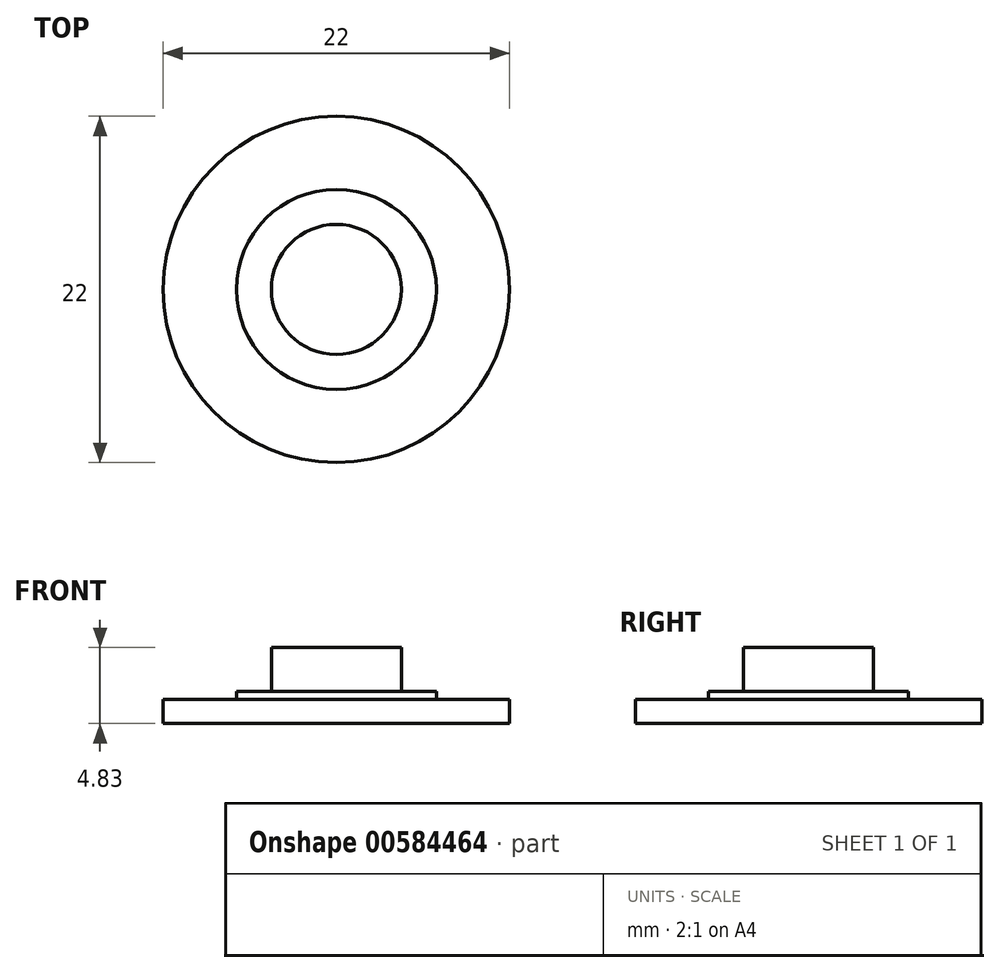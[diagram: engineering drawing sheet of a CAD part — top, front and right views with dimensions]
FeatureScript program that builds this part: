
annotation { "Feature Type Name" : "Feature", "Feature Type Description" : "" }
export const myFeature = defineFeature(function(context is Context, id is Id, definition is map)
    precondition{}
    {
        {
            var Q0;
            Q0=qCreatedBy(makeId("Top.planeOp"),FACE);
            var sketch = newSketch(context, id + "F0", { "sketchPlane" : qUnion([Q0])});
            skCircle(sketch, "E0", {"center": v(0, 0) * mm, "radius": 11 * mm});
            skSolve(sketch);
        }
        {
            var Q0;
            Q0=qSketchRegion(id+"F0",true);
            extrude(context, id + "F1", {"entities" : qUnion([Q0]), "depth" : 1.52 * mm, "offsetDistance" : 25.4 * mm});
        }
        {
            var Q0;
            Q0=makeQuery(id+"F1.opExtrude","CAP_FACE",FACE,{"disambiguationData":[OSD([sQuery(id+"F0.wireOp",EDGE,"E0")])],"isStart":false});
            var sketch = newSketch(context, id + "F2", { "sketchPlane" : qUnion([Q0])});
            skCircle(sketch, "E1", {"center": v(0, 0) * mm, "radius": 6.35 * mm});
            skSolve(sketch);
        }
        {
            var Q0;
            Q0=qSketchRegion(id+"F2",true);
            extrude(context, id + "F3", {"entities" : qUnion([Q0]), "operationType" : NewBodyOperationType.ADD, "depth" : 0.5 * mm, "offsetDistance" : 25.4 * mm});
        }
        {
            var Q0;
            Q0=makeQuery(id+"F3.opExtrude","CAP_FACE",FACE,{"disambiguationData":[OSD([sQuery(id+"F2.wireOp",EDGE,"E1")])],"isStart":false});
            var sketch = newSketch(context, id + "F4", { "sketchPlane" : qUnion([Q0])});
            skCircle(sketch, "E2", {"center": v(0, 0) * mm, "radius": 4.13 * mm});
            skSolve(sketch);
        }
        {
            var Q0;
            Q0=makeQuery(id+"F4.imprint","IMPRINT",FACE,{"disambiguationData":[TD([[makeQuery(id+"F4.imprint","IMPRINT",EDGE,{"derivedFrom":sQuery(id+"F4.wireOp",EDGE,"E2")}),1.0]])]});
            var Q1;
            Q1=sQuery(id+"F4.wireOp",EDGE,"E2");
            extrude(context, id + "F5", {"entities" : qUnion([Q0]), "operationType" : NewBodyOperationType.ADD, "surfaceEntities" : qUnion([Q1]), "depth" : 2.8 * mm, "offsetDistance" : 25.4 * mm});
        }
    });
